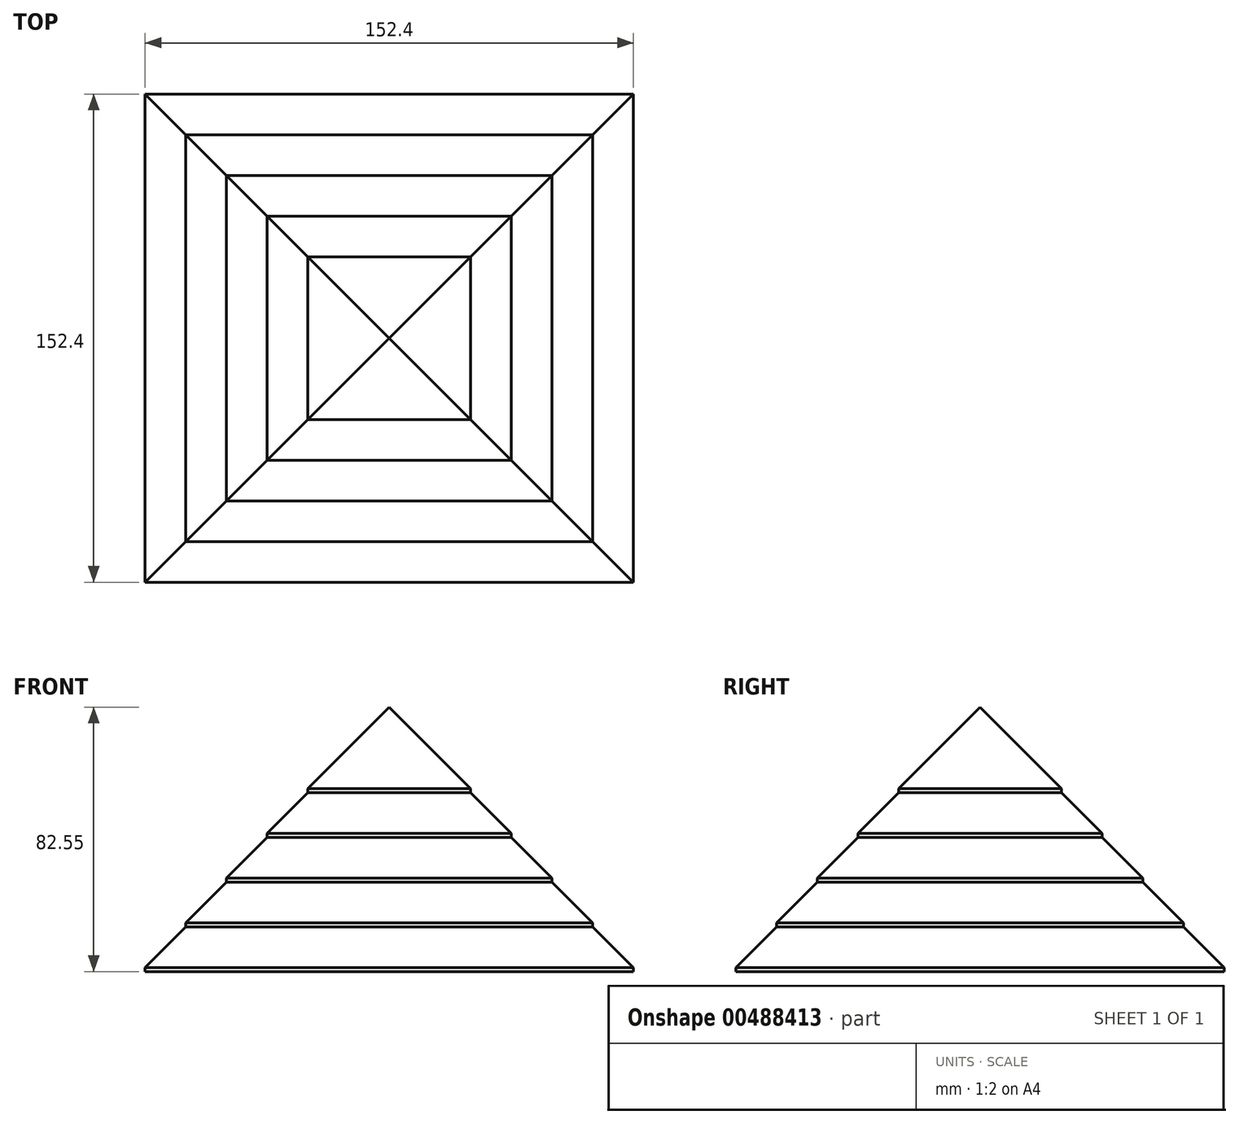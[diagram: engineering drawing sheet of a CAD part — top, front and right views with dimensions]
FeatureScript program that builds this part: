
annotation { "Feature Type Name" : "Feature", "Feature Type Description" : "" }
export const myFeature = defineFeature(function(context is Context, id is Id, definition is map)
    precondition{}
    {
        {
            var Q0;
            Q0=qCreatedBy(makeId("Top.planeOp"),FACE);
            var sketch = newSketch(context, id + "F0", { "sketchPlane" : qUnion([Q0])});
            skLineSegment(sketch, "E0.bottom", {"start": v(0, 0) * mm, "end": v(-76.2, 0) * mm});
            skLineSegment(sketch, "E0.top", {"start": v(0, 76.2) * mm, "end": v(-76.2, 76.2) * mm});
            skLineSegment(sketch, "E0.left", {"start": v(0, 0) * mm, "end": v(0, 76.2) * mm});
            skLineSegment(sketch, "E0.right", {"start": v(-76.2, 0) * mm, "end": v(-76.2, 76.2) * mm});
            skLineSegment(sketch, "E1.bottom", {"start": v(0, 0) * mm, "end": v(76.2, 0) * mm});
            skLineSegment(sketch, "E1.top", {"start": v(0, 76.2) * mm, "end": v(76.2, 76.2) * mm});
            skLineSegment(sketch, "E1.right", {"start": v(76.2, 0) * mm, "end": v(76.2, 76.2) * mm});
            skLineSegment(sketch, "E2.top", {"start": v(0, -76.2) * mm, "end": v(76.2, -76.2) * mm});
            skLineSegment(sketch, "E2.left", {"start": v(0, 0) * mm, "end": v(0, -76.2) * mm});
            skLineSegment(sketch, "E2.right", {"start": v(76.2, 0) * mm, "end": v(76.2, -76.2) * mm});
            skLineSegment(sketch, "E3.top", {"start": v(0, -76.2) * mm, "end": v(-76.2, -76.2) * mm});
            skLineSegment(sketch, "E3.right", {"start": v(-76.2, 0) * mm, "end": v(-76.2, -76.2) * mm});
            skSolve(sketch);
        }
        {
            var Q0;
            Q0=makeQuery(id+"F0.imprint","IMPRINT",FACE,{"disambiguationData":[TD([[makeQuery(id+"F0.imprint","IMPRINT",EDGE,{"derivedFrom":sQuery(id+"F0.wireOp",EDGE,"E1.top")}),-1.0]])]});
            var Q1;
            Q1=makeQuery(id+"F0.imprint","IMPRINT",FACE,{"disambiguationData":[TD([[makeQuery(id+"F0.imprint","IMPRINT",EDGE,{"derivedFrom":sQuery(id+"F0.wireOp",EDGE,"E1.bottom")}),-1.0]])]});
            var Q2;
            Q2=makeQuery(id+"F0.imprint","IMPRINT",FACE,{"disambiguationData":[TD([[makeQuery(id+"F0.imprint","IMPRINT",EDGE,{"derivedFrom":sQuery(id+"F0.wireOp",EDGE,"E0.bottom")}),1.0]])]});
            var Q3;
            Q3=makeQuery(id+"F0.imprint","IMPRINT",FACE,{"disambiguationData":[TD([[makeQuery(id+"F0.imprint","IMPRINT",EDGE,{"derivedFrom":sQuery(id+"F0.wireOp",EDGE,"E0.top")}),1.0]])]});
            extrude(context, id + "F1", {"entities" : qUnion([Q0, Q1, Q2, Q3]), "depth" : 13.97 * mm});
        }
        {
            var Q0;
            Q0=makeQuery(id+"F1.opExtrude","CAP_FACE",FACE,{"disambiguationData":[OSD([sQuery(id+"F0.wireOp",EDGE,"E0.top"),sQuery(id+"F0.wireOp",EDGE,"E0.right"),sQuery(id+"F0.wireOp",EDGE,"E1.top"),sQuery(id+"F0.wireOp",EDGE,"E1.right"),sQuery(id+"F0.wireOp",EDGE,"E2.top"),sQuery(id+"F0.wireOp",EDGE,"E2.right"),sQuery(id+"F0.wireOp",EDGE,"E3.top"),sQuery(id+"F0.wireOp",EDGE,"E3.right")])],"isStart":false});
            var sketch = newSketch(context, id + "F2", { "sketchPlane" : qUnion([Q0])});
            skLineSegment(sketch, "E4.bottom", {"start": v(0, 0) * mm, "end": v(-63.5, 0) * mm});
            skLineSegment(sketch, "E4.top", {"start": v(0, 63.5) * mm, "end": v(-63.5, 63.5) * mm});
            skLineSegment(sketch, "E4.left", {"start": v(0, 0) * mm, "end": v(0, 63.5) * mm});
            skLineSegment(sketch, "E4.right", {"start": v(-63.5, 0) * mm, "end": v(-63.5, 63.5) * mm});
            skLineSegment(sketch, "E5.bottom", {"start": v(0, 0) * mm, "end": v(63.5, 0) * mm});
            skLineSegment(sketch, "E5.top", {"start": v(0, -63.5) * mm, "end": v(63.5, -63.5) * mm});
            skLineSegment(sketch, "E5.left", {"start": v(0, 0) * mm, "end": v(0, -63.5) * mm});
            skLineSegment(sketch, "E5.right", {"start": v(63.5, 0) * mm, "end": v(63.5, -63.5) * mm});
            skLineSegment(sketch, "E6.top", {"start": v(0, 63.5) * mm, "end": v(63.5, 63.5) * mm});
            skLineSegment(sketch, "E6.right", {"start": v(63.5, 0) * mm, "end": v(63.5, 63.5) * mm});
            skLineSegment(sketch, "E7.top", {"start": v(0, -63.5) * mm, "end": v(-63.5, -63.5) * mm});
            skLineSegment(sketch, "E7.right", {"start": v(-63.5, 0) * mm, "end": v(-63.5, -63.5) * mm});
            skSolve(sketch);
        }
        {
            var Q0;
            Q0 = qSketchRegion(id + "F2", true);
            extrude(context, id + "F3", {"entities" : qUnion([Q0]), "operationType" : NewBodyOperationType.ADD, "depth" : 13.97 * mm});
        }
        {
            var Q0;
            Q0=makeQuery(id+"F3.opExtrude","CAP_FACE",FACE,{"disambiguationData":[OSD([sQuery(id+"F2.wireOp",EDGE,"E4.top"),sQuery(id+"F2.wireOp",EDGE,"E4.right"),sQuery(id+"F2.wireOp",EDGE,"E5.top"),sQuery(id+"F2.wireOp",EDGE,"E5.right"),sQuery(id+"F2.wireOp",EDGE,"E6.top"),sQuery(id+"F2.wireOp",EDGE,"E6.right"),sQuery(id+"F2.wireOp",EDGE,"E7.top"),sQuery(id+"F2.wireOp",EDGE,"E7.right")])],"isStart":false});
            var sketch = newSketch(context, id + "F4", { "sketchPlane" : qUnion([Q0])});
            skLineSegment(sketch, "E8.bottom", {"start": v(0, 0) * mm, "end": v(-50.8, 0) * mm});
            skLineSegment(sketch, "E8.top", {"start": v(0, 50.8) * mm, "end": v(-50.8, 50.8) * mm});
            skLineSegment(sketch, "E8.left", {"start": v(0, 0) * mm, "end": v(0, 50.8) * mm});
            skLineSegment(sketch, "E8.right", {"start": v(-50.8, 0) * mm, "end": v(-50.8, 50.8) * mm});
            skLineSegment(sketch, "E9.bottom", {"start": v(0, 0) * mm, "end": v(50.8, 0) * mm});
            skLineSegment(sketch, "E9.top", {"start": v(0, 50.8) * mm, "end": v(50.8, 50.8) * mm});
            skLineSegment(sketch, "E9.right", {"start": v(50.8, 0) * mm, "end": v(50.8, 50.8) * mm});
            skLineSegment(sketch, "E10.top", {"start": v(0, -50.8) * mm, "end": v(50.8, -50.8) * mm});
            skLineSegment(sketch, "E10.left", {"start": v(0, 0) * mm, "end": v(0, -50.8) * mm});
            skLineSegment(sketch, "E10.right", {"start": v(50.8, 0) * mm, "end": v(50.8, -50.8) * mm});
            skLineSegment(sketch, "E11.top", {"start": v(0, -50.8) * mm, "end": v(-50.8, -50.8) * mm});
            skLineSegment(sketch, "E11.right", {"start": v(-50.8, 0) * mm, "end": v(-50.8, -50.8) * mm});
            skSolve(sketch);
        }
        {
            var Q0;
            Q0 = qSketchRegion(id + "F4", true);
            extrude(context, id + "F5", {"entities" : qUnion([Q0]), "operationType" : NewBodyOperationType.ADD, "depth" : 13.97 * mm});
        }
        {
            var Q0;
            Q0=makeQuery(id+"F5.opExtrude","CAP_FACE",FACE,{"disambiguationData":[OSD([sQuery(id+"F4.wireOp",EDGE,"E8.top"),sQuery(id+"F4.wireOp",EDGE,"E8.right"),sQuery(id+"F4.wireOp",EDGE,"E9.top"),sQuery(id+"F4.wireOp",EDGE,"E9.right"),sQuery(id+"F4.wireOp",EDGE,"E10.top"),sQuery(id+"F4.wireOp",EDGE,"E10.right"),sQuery(id+"F4.wireOp",EDGE,"E11.top"),sQuery(id+"F4.wireOp",EDGE,"E11.right")])],"isStart":false});
            var sketch = newSketch(context, id + "F6", { "sketchPlane" : qUnion([Q0])});
            skLineSegment(sketch, "E12.bottom", {"start": v(0, 0) * mm, "end": v(-38.1, 0) * mm});
            skLineSegment(sketch, "E12.top", {"start": v(0, 38.1) * mm, "end": v(-38.1, 38.1) * mm});
            skLineSegment(sketch, "E12.left", {"start": v(0, 0) * mm, "end": v(0, 38.1) * mm});
            skLineSegment(sketch, "E12.right", {"start": v(-38.1, 0) * mm, "end": v(-38.1, 38.1) * mm});
            skLineSegment(sketch, "E13.bottom", {"start": v(0, 0) * mm, "end": v(38.1, 0) * mm});
            skLineSegment(sketch, "E13.top", {"start": v(0, -38.1) * mm, "end": v(38.1, -38.1) * mm});
            skLineSegment(sketch, "E13.left", {"start": v(0, 0) * mm, "end": v(0, -38.1) * mm});
            skLineSegment(sketch, "E13.right", {"start": v(38.1, 0) * mm, "end": v(38.1, -38.1) * mm});
            skLineSegment(sketch, "E14.top", {"start": v(0, -38.1) * mm, "end": v(-38.1, -38.1) * mm});
            skLineSegment(sketch, "E14.right", {"start": v(-38.1, 0) * mm, "end": v(-38.1, -38.1) * mm});
            skLineSegment(sketch, "E15.top", {"start": v(0, 38.1) * mm, "end": v(38.1, 38.1) * mm});
            skLineSegment(sketch, "E15.right", {"start": v(38.1, 0) * mm, "end": v(38.1, 38.1) * mm});
            skSolve(sketch);
        }
        {
            var Q0;
            Q0=makeQuery(id+"F6.imprint","IMPRINT",FACE,{"disambiguationData":[TD([[makeQuery(id+"F6.imprint","IMPRINT",EDGE,{"derivedFrom":sQuery(id+"F6.wireOp",EDGE,"E13.top")}),1.0]])]});
            var Q1;
            Q1=makeQuery(id+"F6.imprint","IMPRINT",FACE,{"disambiguationData":[TD([[makeQuery(id+"F6.imprint","IMPRINT",EDGE,{"derivedFrom":sQuery(id+"F6.wireOp",EDGE,"E12.bottom")}),1.0]])]});
            var Q2;
            Q2=makeQuery(id+"F6.imprint","IMPRINT",FACE,{"disambiguationData":[TD([[makeQuery(id+"F6.imprint","IMPRINT",EDGE,{"derivedFrom":sQuery(id+"F6.wireOp",EDGE,"E13.bottom")}),1.0]])]});
            var Q3;
            Q3=makeQuery(id+"F6.imprint","IMPRINT",FACE,{"disambiguationData":[TD([[makeQuery(id+"F6.imprint","IMPRINT",EDGE,{"derivedFrom":sQuery(id+"F6.wireOp",EDGE,"E12.top")}),1.0]])]});
            extrude(context, id + "F7", {"entities" : qUnion([Q0, Q1, Q2, Q3]), "operationType" : NewBodyOperationType.ADD, "depth" : 13.97 * mm});
        }
        {
            var Q0;
            Q0=makeQuery(id+"F7.opExtrude","CAP_FACE",FACE,{"disambiguationData":[OSD([sQuery(id+"F6.wireOp",EDGE,"E12.top"),sQuery(id+"F6.wireOp",EDGE,"E12.right"),sQuery(id+"F6.wireOp",EDGE,"E13.top"),sQuery(id+"F6.wireOp",EDGE,"E13.right"),sQuery(id+"F6.wireOp",EDGE,"E14.top"),sQuery(id+"F6.wireOp",EDGE,"E14.right"),sQuery(id+"F6.wireOp",EDGE,"E15.top"),sQuery(id+"F6.wireOp",EDGE,"E15.right")])],"isStart":false});
            var sketch = newSketch(context, id + "F8", { "sketchPlane" : qUnion([Q0])});
            skLineSegment(sketch, "E16.bottom", {"start": v(0, 0) * mm, "end": v(-25.4, 0) * mm});
            skLineSegment(sketch, "E16.top", {"start": v(0, 25.4) * mm, "end": v(-25.4, 25.4) * mm});
            skLineSegment(sketch, "E16.left", {"start": v(0, 0) * mm, "end": v(0, 25.4) * mm});
            skLineSegment(sketch, "E16.right", {"start": v(-25.4, 0) * mm, "end": v(-25.4, 25.4) * mm});
            skLineSegment(sketch, "E17.bottom", {"start": v(0, 0) * mm, "end": v(25.4, 0) * mm});
            skLineSegment(sketch, "E17.top", {"start": v(0, 25.4) * mm, "end": v(25.4, 25.4) * mm});
            skLineSegment(sketch, "E17.right", {"start": v(25.4, 0) * mm, "end": v(25.4, 25.4) * mm});
            skLineSegment(sketch, "E18.top", {"start": v(0, -25.4) * mm, "end": v(25.4, -25.4) * mm});
            skLineSegment(sketch, "E18.left", {"start": v(0, 0) * mm, "end": v(0, -25.4) * mm});
            skLineSegment(sketch, "E18.right", {"start": v(25.4, 0) * mm, "end": v(25.4, -25.4) * mm});
            skLineSegment(sketch, "E19.top", {"start": v(0, -25.4) * mm, "end": v(-25.4, -25.4) * mm});
            skLineSegment(sketch, "E19.right", {"start": v(-25.4, 0) * mm, "end": v(-25.4, -25.4) * mm});
            skSolve(sketch);
        }
        {
            var Q0;
            Q0 = qSketchRegion(id + "F8", true);
            extrude(context, id + "F9", {"entities" : qUnion([Q0]), "operationType" : NewBodyOperationType.ADD, "depth" : 13.97 * mm});
        }
        {
            var Q0;
            Q0=makeQuery(id+"F9.opExtrude","CAP_EDGE",EDGE,{"disambiguationData":[OSD([sQuery(id+"F8.wireOp",EDGE,"E16.right"),sQuery(id+"F8.wireOp",EDGE,"E19.right")])],"isStart":false});
            var Q1;
            Q1=makeQuery(id+"F9.opExtrude","CAP_EDGE",EDGE,{"disambiguationData":[OSD([sQuery(id+"F8.wireOp",EDGE,"E18.top"),sQuery(id+"F8.wireOp",EDGE,"E19.top")])],"isStart":false});
            var Q2;
            Q2=makeQuery(id+"F9.opExtrude","CAP_EDGE",EDGE,{"disambiguationData":[OSD([sQuery(id+"F8.wireOp",EDGE,"E17.right"),sQuery(id+"F8.wireOp",EDGE,"E18.right")])],"isStart":false});
            var Q3;
            Q3=makeQuery(id+"F9.opExtrude","CAP_EDGE",EDGE,{"disambiguationData":[OSD([sQuery(id+"F8.wireOp",EDGE,"E16.top"),sQuery(id+"F8.wireOp",EDGE,"E17.top")])],"isStart":false});
            var Q4;
            Q4=makeQuery(id+"F7.opExtrude","CAP_EDGE",EDGE,{"disambiguationData":[OSD([sQuery(id+"F6.wireOp",EDGE,"E12.top"),sQuery(id+"F6.wireOp",EDGE,"E15.top")])],"isStart":false});
            var Q5;
            Q5=makeQuery(id+"F7.opExtrude","CAP_EDGE",EDGE,{"disambiguationData":[OSD([sQuery(id+"F6.wireOp",EDGE,"E12.right"),sQuery(id+"F6.wireOp",EDGE,"E14.right")])],"isStart":false});
            var Q6;
            Q6=makeQuery(id+"F7.opExtrude","CAP_EDGE",EDGE,{"disambiguationData":[OSD([sQuery(id+"F6.wireOp",EDGE,"E13.top"),sQuery(id+"F6.wireOp",EDGE,"E14.top")])],"isStart":false});
            var Q7;
            Q7=makeQuery(id+"F7.opExtrude","CAP_EDGE",EDGE,{"disambiguationData":[OSD([sQuery(id+"F6.wireOp",EDGE,"E13.right"),sQuery(id+"F6.wireOp",EDGE,"E15.right")])],"isStart":false});
            var Q8;
            Q8=makeQuery(id+"F5.opExtrude","CAP_EDGE",EDGE,{"disambiguationData":[OSD([sQuery(id+"F4.wireOp",EDGE,"E9.right"),sQuery(id+"F4.wireOp",EDGE,"E10.right")])],"isStart":false});
            var Q9;
            Q9=makeQuery(id+"F5.opExtrude","CAP_EDGE",EDGE,{"disambiguationData":[OSD([sQuery(id+"F4.wireOp",EDGE,"E8.top"),sQuery(id+"F4.wireOp",EDGE,"E9.top")])],"isStart":false});
            var Q10;
            Q10=makeQuery(id+"F5.opExtrude","CAP_EDGE",EDGE,{"disambiguationData":[OSD([sQuery(id+"F4.wireOp",EDGE,"E8.right"),sQuery(id+"F4.wireOp",EDGE,"E11.right")])],"isStart":false});
            var Q11;
            Q11=makeQuery(id+"F5.opExtrude","CAP_EDGE",EDGE,{"disambiguationData":[OSD([sQuery(id+"F4.wireOp",EDGE,"E10.top"),sQuery(id+"F4.wireOp",EDGE,"E11.top")])],"isStart":false});
            var Q12;
            Q12=makeQuery(id+"F3.opExtrude","CAP_EDGE",EDGE,{"disambiguationData":[OSD([sQuery(id+"F2.wireOp",EDGE,"E4.right"),sQuery(id+"F2.wireOp",EDGE,"E7.right")])],"isStart":false});
            var Q13;
            Q13=makeQuery(id+"F3.opExtrude","CAP_EDGE",EDGE,{"disambiguationData":[OSD([sQuery(id+"F2.wireOp",EDGE,"E4.top"),sQuery(id+"F2.wireOp",EDGE,"E6.top")])],"isStart":false});
            var Q14;
            Q14=makeQuery(id+"F3.opExtrude","CAP_EDGE",EDGE,{"disambiguationData":[OSD([sQuery(id+"F2.wireOp",EDGE,"E5.right"),sQuery(id+"F2.wireOp",EDGE,"E6.right")])],"isStart":false});
            var Q15;
            Q15=makeQuery(id+"F3.opExtrude","CAP_EDGE",EDGE,{"disambiguationData":[OSD([sQuery(id+"F2.wireOp",EDGE,"E5.top"),sQuery(id+"F2.wireOp",EDGE,"E7.top")])],"isStart":false});
            var Q16;
            Q16=makeQuery(id+"F1.opExtrude","CAP_EDGE",EDGE,{"disambiguationData":[OSD([sQuery(id+"F0.wireOp",EDGE,"E1.right"),sQuery(id+"F0.wireOp",EDGE,"E2.right")])],"isStart":false});
            var Q17;
            Q17=makeQuery(id+"F1.opExtrude","CAP_EDGE",EDGE,{"disambiguationData":[OSD([sQuery(id+"F0.wireOp",EDGE,"E0.top"),sQuery(id+"F0.wireOp",EDGE,"E1.top")])],"isStart":false});
            var Q18;
            Q18=makeQuery(id+"F1.opExtrude","CAP_EDGE",EDGE,{"disambiguationData":[OSD([sQuery(id+"F0.wireOp",EDGE,"E0.right"),sQuery(id+"F0.wireOp",EDGE,"E3.right")])],"isStart":false});
            var Q19;
            Q19=makeQuery(id+"F1.opExtrude","CAP_EDGE",EDGE,{"disambiguationData":[OSD([sQuery(id+"F0.wireOp",EDGE,"E2.top"),sQuery(id+"F0.wireOp",EDGE,"E3.top")])],"isStart":false});
            chamfer(context, id + "F10", {"entities" : qUnion([Q0, Q1, Q2, Q3, Q4, Q5, Q6, Q7, Q8, Q9, Q10, Q11, Q12, Q13, Q14, Q15, Q16, Q17, Q18, Q19]), "width" : 12.7 * mm, "tangentPropagation" : true});
        }
        {
            var Q0;
            Q0=makeQuery(id+"F9.opExtrude","CAP_FACE",FACE,{"disambiguationData":[OSD([sQuery(id+"F8.wireOp",EDGE,"E16.top"),sQuery(id+"F8.wireOp",EDGE,"E16.right"),sQuery(id+"F8.wireOp",EDGE,"E17.top"),sQuery(id+"F8.wireOp",EDGE,"E17.right"),sQuery(id+"F8.wireOp",EDGE,"E18.top"),sQuery(id+"F8.wireOp",EDGE,"E18.right"),sQuery(id+"F8.wireOp",EDGE,"E19.top"),sQuery(id+"F8.wireOp",EDGE,"E19.right")])],"isStart":false});
            cPlane(context, id + "F11", {"entities" : qUnion([Q0]), "cplaneType" : CPlaneType.OFFSET, "offset" : 12.7 * mm, "width" : 152.4 * mm, "height" : 152.4 * mm});
        }
        {
            var Q0;
            Q0=qCreatedBy(id+"F11.planeOp",FACE);
            var sketch = newSketch(context, id + "F12", { "sketchPlane" : qUnion([Q0])});
            skPoint(sketch, "E20", {"position": v(0, 0) * mm});
            skSolve(sketch);
        }
        {
            var Q1;
            Q1=makeQuery(id+"F9.opExtrude","CAP_FACE",FACE,{"disambiguationData":[OSD([sQuery(id+"F8.wireOp",EDGE,"E16.top"),sQuery(id+"F8.wireOp",EDGE,"E16.right"),sQuery(id+"F8.wireOp",EDGE,"E17.top"),sQuery(id+"F8.wireOp",EDGE,"E17.right"),sQuery(id+"F8.wireOp",EDGE,"E18.top"),sQuery(id+"F8.wireOp",EDGE,"E18.right"),sQuery(id+"F8.wireOp",EDGE,"E19.top"),sQuery(id+"F8.wireOp",EDGE,"E19.right")])],"isStart":false});
            var Q2;
            Q2=sQuery(id+"F12.wireOp",VERTEX,"E20");
            loft(context, id + "F13", {"operationType" : NewBodyOperationType.ADD, "sheetProfilesArray" : [{ "sheetProfileEntities" : qUnion([Q1]) }, { "sheetProfileEntities" : qUnion([Q2]) }]});
        }
    });
